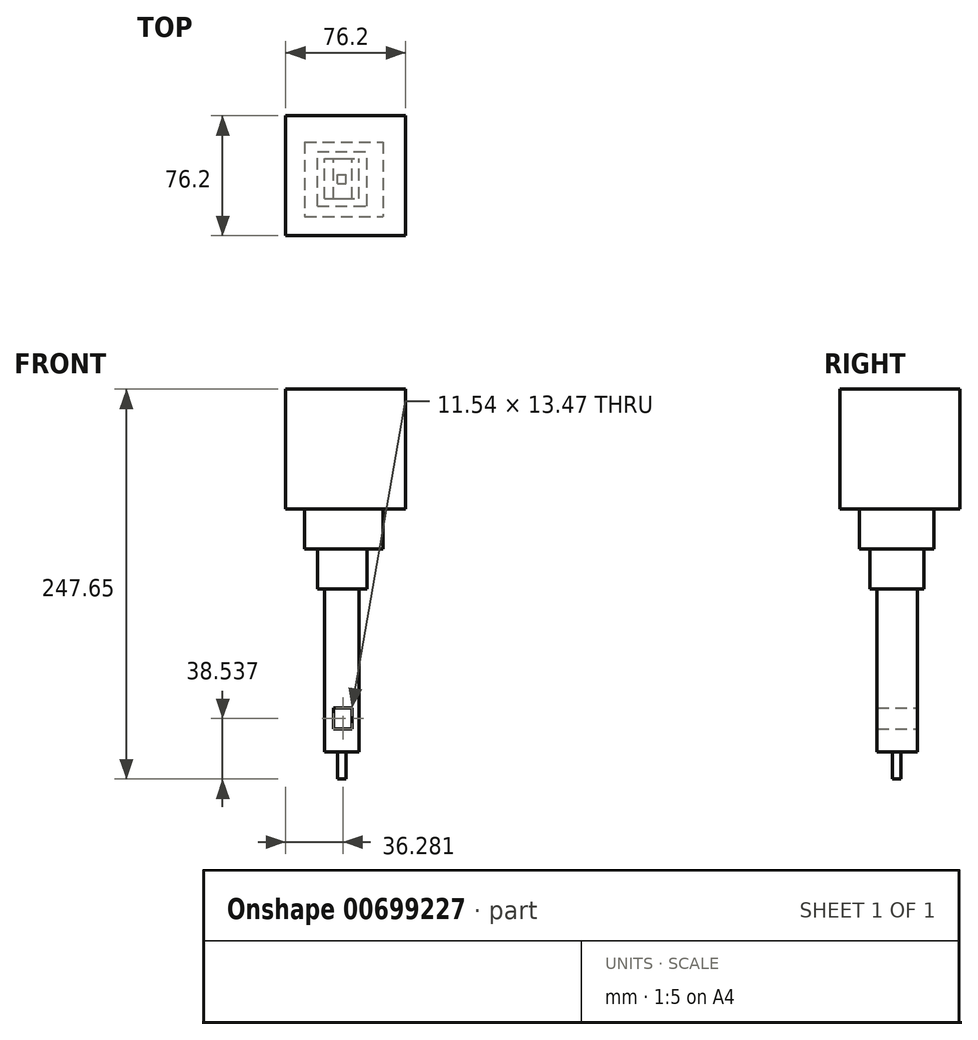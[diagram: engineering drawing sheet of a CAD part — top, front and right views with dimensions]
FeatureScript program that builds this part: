
annotation { "Feature Type Name" : "Feature", "Feature Type Description" : "" }
export const myFeature = defineFeature(function(context is Context, id is Id, definition is map)
    precondition{}
    {
        {
            var Q0;
            Q0=qCreatedBy(makeId("Front.planeOp"),FACE);
            var sketch = newSketch(context, id + "F0", { "sketchPlane" : qUnion([Q0])});
            skLineSegment(sketch, "E0.bottom", {"start": v(0, 0) * mm, "end": v(-76.2, 0) * mm});
            skLineSegment(sketch, "E0.top", {"start": v(0, 76.2) * mm, "end": v(-76.2, 76.2) * mm});
            skLineSegment(sketch, "E0.left", {"start": v(0, 0) * mm, "end": v(0, 76.2) * mm});
            skLineSegment(sketch, "E0.right", {"start": v(-76.2, 0) * mm, "end": v(-76.2, 76.2) * mm});
            skSolve(sketch);
        }
        {
            var Q0;
            Q0 = qSketchRegion(id + "F0", true);
            extrude(context, id + "F1", {"entities" : qUnion([Q0]), "depth" : 76.2 * mm, "offsetDistance" : 25.4 * mm});
        }
        {
            var Q0;
            Q0=qCreatedBy(makeId("Top.planeOp"),FACE);
            var sketch = newSketch(context, id + "F2", { "sketchPlane" : qUnion([Q0])});
            skLineSegment(sketch, "E1.bottom", {"start": v(-64.23, -16.57) * mm, "end": v(-14.5, -16.57) * mm});
            skLineSegment(sketch, "E1.top", {"start": v(-64.23, -63.93) * mm, "end": v(-14.5, -63.93) * mm});
            skLineSegment(sketch, "E1.left", {"start": v(-64.23, -16.57) * mm, "end": v(-64.23, -63.93) * mm});
            skLineSegment(sketch, "E1.right", {"start": v(-14.5, -16.57) * mm, "end": v(-14.5, -63.93) * mm});
            skPoint(sketch, "E1.middle", {"position": v(-39.36, -40.25) * mm});
            skSolve(sketch);
        }
        {
            var Q0;
            Q0 = qSketchRegion(id + "F2", true);
            extrude(context, id + "F3", {"entities" : qUnion([Q0]), "operationType" : NewBodyOperationType.ADD, "oppositeDirection" : true, "depth" : 25.4 * mm, "offsetDistance" : 25.4 * mm});
        }
        {
            var Q0;
            Q0=qCreatedBy(makeId("Top.planeOp"),FACE);
            var sketch = newSketch(context, id + "F4", { "sketchPlane" : qUnion([Q0])});
            skLineSegment(sketch, "E2.bottom", {"start": v(-56.14, -57.22) * mm, "end": v(-24.57, -57.22) * mm});
            skLineSegment(sketch, "E2.top", {"start": v(-56.14, -22.89) * mm, "end": v(-24.57, -22.89) * mm});
            skLineSegment(sketch, "E2.left", {"start": v(-56.14, -57.22) * mm, "end": v(-56.14, -22.89) * mm});
            skLineSegment(sketch, "E2.right", {"start": v(-24.57, -57.22) * mm, "end": v(-24.57, -22.89) * mm});
            skPoint(sketch, "E2.middle", {"position": v(-40.35, -40.05) * mm});
            skSolve(sketch);
        }
        {
            var Q0;
            Q0 = qSketchRegion(id + "F4", true);
            extrude(context, id + "F5", {"entities" : qUnion([Q0]), "operationType" : NewBodyOperationType.ADD, "oppositeDirection" : true, "depth" : 50.8 * mm, "offsetDistance" : 25.4 * mm});
        }
        {
            var Q0;
            Q0=qCreatedBy(makeId("Top.planeOp"),FACE);
            var sketch = newSketch(context, id + "F6", { "sketchPlane" : qUnion([Q0])});
            skLineSegment(sketch, "E3.bottom", {"start": v(-51.6, -52.68) * mm, "end": v(-29.5, -52.68) * mm});
            skLineSegment(sketch, "E3.top", {"start": v(-51.6, -27.03) * mm, "end": v(-29.5, -27.03) * mm});
            skLineSegment(sketch, "E3.left", {"start": v(-51.6, -52.68) * mm, "end": v(-51.6, -27.03) * mm});
            skLineSegment(sketch, "E3.right", {"start": v(-29.5, -52.68) * mm, "end": v(-29.5, -27.03) * mm});
            skPoint(sketch, "E3.middle", {"position": v(-40.55, -39.86) * mm});
            skSolve(sketch);
        }
        {
            var Q0;
            Q0 = qSketchRegion(id + "F6", true);
            extrude(context, id + "F7", {"entities" : qUnion([Q0]), "operationType" : NewBodyOperationType.ADD, "oppositeDirection" : true, "depth" : 154.18 * mm, "offsetDistance" : 25.4 * mm});
        }
        {
            var Q0;
            Q0=qCreatedBy(makeId("Top.planeOp"),FACE);
            var sketch = newSketch(context, id + "F8", { "sketchPlane" : qUnion([Q0])});
            skLineSegment(sketch, "E4.bottom", {"start": v(-43.3, -43.01) * mm, "end": v(-37.79, -43.01) * mm});
            skLineSegment(sketch, "E4.top", {"start": v(-43.3, -37.49) * mm, "end": v(-37.79, -37.49) * mm});
            skLineSegment(sketch, "E4.left", {"start": v(-43.3, -43.01) * mm, "end": v(-43.3, -37.49) * mm});
            skLineSegment(sketch, "E4.right", {"start": v(-37.79, -43.01) * mm, "end": v(-37.79, -37.49) * mm});
            skPoint(sketch, "E4.middle", {"position": v(-40.55, -40.25) * mm});
            skSolve(sketch);
        }
        {
            var Q0;
            Q0 = qSketchRegion(id + "F8", true);
            extrude(context, id + "F9", {"entities" : qUnion([Q0]), "operationType" : NewBodyOperationType.ADD, "oppositeDirection" : true, "depth" : 171.45 * mm, "offsetDistance" : 25.4 * mm});
        }
        {
            var Q0;
            Q0=qCreatedBy(makeId("Front.planeOp"),FACE);
            var sketch = newSketch(context, id + "F10", { "sketchPlane" : qUnion([Q0])});
            skLineSegment(sketch, "E5.bottom", {"start": v(-34.15, -126.18) * mm, "end": v(-45.7, -126.18) * mm});
            skLineSegment(sketch, "E5.top", {"start": v(-34.15, -139.65) * mm, "end": v(-45.7, -139.65) * mm});
            skLineSegment(sketch, "E5.left", {"start": v(-34.15, -126.18) * mm, "end": v(-34.15, -139.65) * mm});
            skLineSegment(sketch, "E5.right", {"start": v(-45.7, -126.18) * mm, "end": v(-45.7, -139.65) * mm});
            skPoint(sketch, "E5.middle", {"position": v(-39.92, -132.91) * mm});
            skSolve(sketch);
        }
        {
            var Q0;
            Q0 = qSketchRegion(id + "F10", true);
            extrude(context, id + "F11", {"entities" : qUnion([Q0]), "operationType" : NewBodyOperationType.REMOVE, "depth" : 96.77 * mm, "offsetDistance" : 25.4 * mm});
        }
    });
